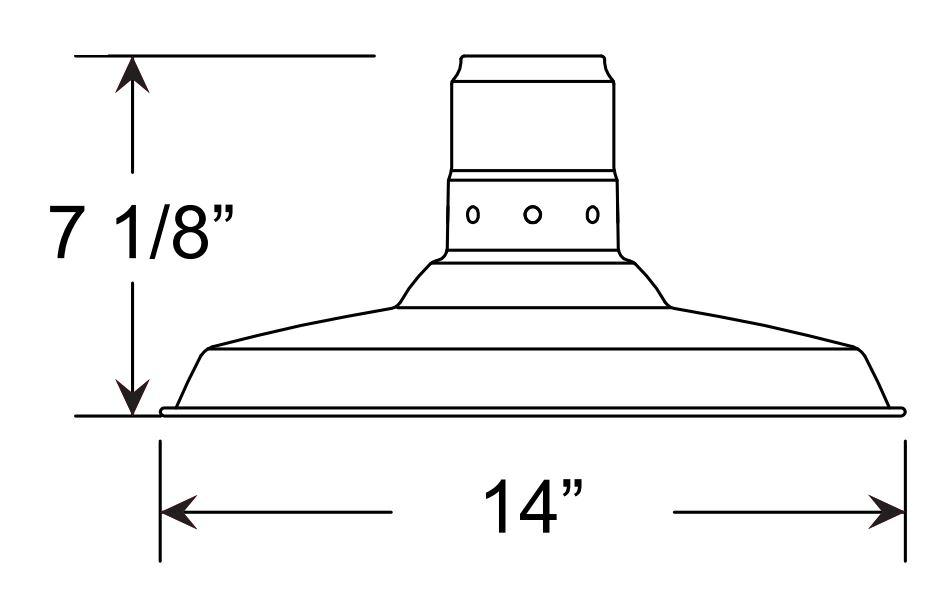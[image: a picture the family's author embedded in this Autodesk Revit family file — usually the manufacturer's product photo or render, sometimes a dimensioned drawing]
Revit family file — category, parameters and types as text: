
# Revit family: Radial 8,12,16,18,20,24 MB
name_source: partatom
category: Lighting Fixtures
units: mm (PartAtom-declared; Revit-internal decimal feet)

## family parameters
Always vertical = Yes
Cut with Voids When Loaded = No
Light Source = Yes
OmniClass Number = 23.80.70.00
OmniClass Title = Lighting
Part Type = Normal
Room Calculation Point = No
Round Connector Dimension = Use Diameter
Shared = No
Work Plane-Based = No

## types (6) — shared parameters
Body Colour = Spun aluminium
Body Material = body
Bulb = Glass
CRI = >90
Canopy Body = body
Color Filter = 16777215
Construction Material = Heavy Duty spun aluminum.
Default Elevation = 0' - 0"
Description = 120-277 Voltage
Dimming = 1%
Dimming Lamp Color Temperature Shift = <None>
Efficiency = 65-125 lumens per watt
INSIDE BODY = Default
Lamp = MB
Life = L70 50,000 hours
Load Classification = Lighting
Manufacturer = ANP Lighting
Photometric Web File = R920-200GLCL-200INC-T15298.IES
Power Factor = 1
Tilt Angle = 90.00°
URL = https://www.anplighting.com
Voltage = 277 V
Warranty = 5 year limited warranty
b = 0' - 2"

## per-type parameters (varying)
| type | Apparent Load | Fixture Diameter | Fixture Height | R908 | R912 | R916 | R918 | R920 | R924 | Wattage Comments | Weight | a |
| R908 | 100 VA | 0' - 8" | 0' - 4 1/2" | Yes | No | No | No | No | No | 100 W Max | 1.0 lbs | 0' - 8 1/2" |
| R912 | 16 VA | 1' - 0" | 0' - 5 1/4" | No | Yes | No | No | No | No | 100 W Max | 1.0 lbs | 0' - 9" |
| R916 | 200 VA | 1' - 4" | 0' - 6 3/4" | No | No | Yes | No | No | No | 200 W Max | 2.0 lbs | 0' - 11" |
| R918 | 200 VA | 1' - 6" | 0' - 7" | No | No | No | Yes | No | No | 200 W Max | 2.0 lbs | 0' - 11" |
| R920 | 200 VA | 1' - 8" | 0' - 7" | No | No | No | No | Yes | No | 200 W Max | 2.5 lbs | 0' - 11" |
| R924 | 200 VA | 2' - 0" | 0' - 7" | No | No | No | No | No | Yes | 200 W Max | 3.0 lbs | 0' - 11" |

note: column(s) folded — value = type name in every type: Model

## geometry (parser evidence)
native form markers: Sweep x44
no freeform markers — native parametric forms only
